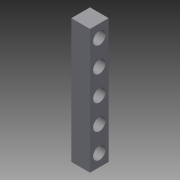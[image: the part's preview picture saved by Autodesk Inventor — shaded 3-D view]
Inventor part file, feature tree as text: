
AUTODESK INVENTOR PART (.ipt)
format: ipt  version: 2015 (Build 190159000, 159)  size: 89,600 bytes
history: native  units: in
note: dims shown in document units (in); Inventor stores cm internally (conversion verified against a paired STEP export)
features: extrude x2, sketch x2
ambient origin geometry x8: Origin, YZ Plane, XZ Plane, XY Plane, X Axis, Y Axis, Z Axis, Center Point
bodies: Solid1 (feature_tree)
feature tree (4):
  extrude  "Extrusion1"  Depth=3.0in
  extrude  "Extrusion3"  Depth=3.0in
  sketch  "Sketch2"  dims[d0=20.0in d1=3.0in]
  sketch  "Sketch4"  dims[d2=3.0in d3=0.0in d10=2.0in d11=2.0in d12=2.0in d13=2.0in d14=2.0in d15=3.0in d16=0.0in]
